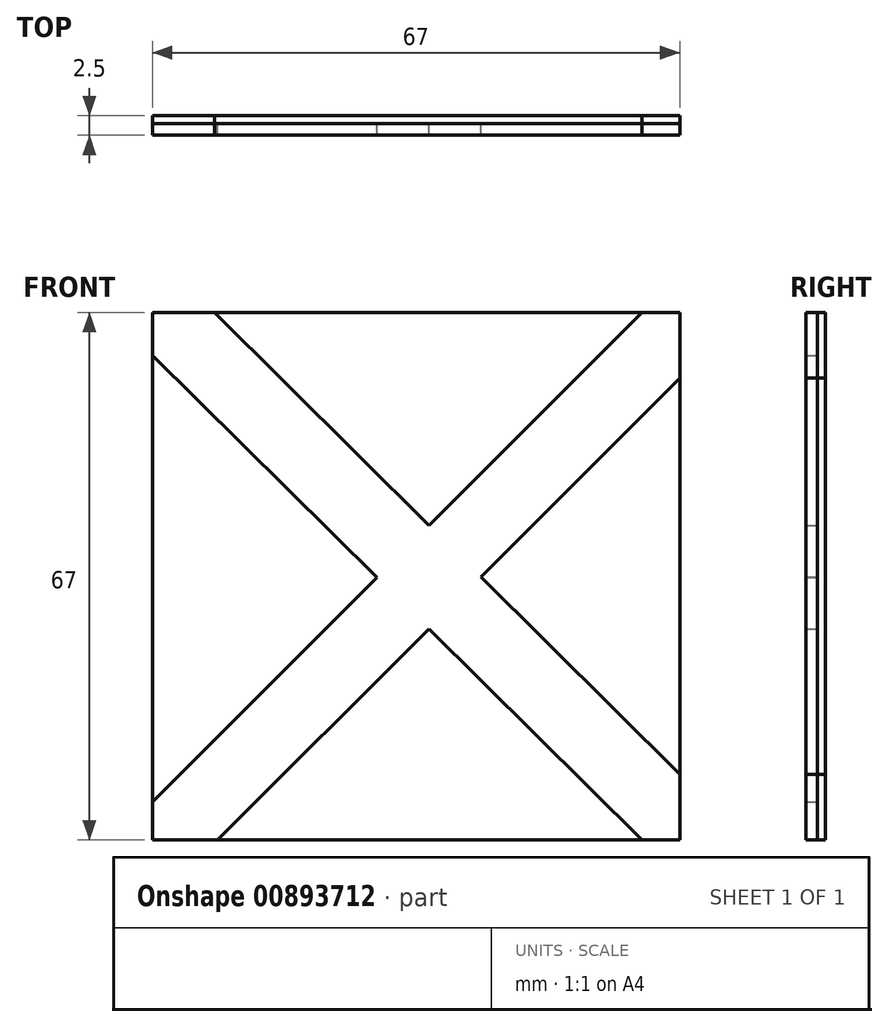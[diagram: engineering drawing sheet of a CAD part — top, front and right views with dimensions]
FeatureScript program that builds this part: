
annotation { "Feature Type Name" : "Feature", "Feature Type Description" : "" }
export const myFeature = defineFeature(function(context is Context, id is Id, definition is map)
    precondition{}
    {
        {
            var Q0;
            Q0=qCreatedBy(makeId("Front.planeOp"),FACE);
            var sketch = newSketch(context, id + "F0", { "sketchPlane" : qUnion([Q0])});
            skLineSegment(sketch, "E0.bottom", {"start": v(33.5, -33.5) * mm, "end": v(-33.5, -33.5) * mm});
            skLineSegment(sketch, "E0.top", {"start": v(33.5, 33.5) * mm, "end": v(-33.5, 33.5) * mm});
            skLineSegment(sketch, "E0.left", {"start": v(33.5, -33.5) * mm, "end": v(33.5, 33.5) * mm});
            skLineSegment(sketch, "E0.right", {"start": v(-33.5, -33.5) * mm, "end": v(-33.5, 33.5) * mm});
            skPoint(sketch, "E0.middle", {"position": v(0, 0) * mm});
            skLineSegment(sketch, "E1", {"start": v(-33.5, -28.7) * mm, "end": v(-4.98, -0.18) * mm});
            skLineSegment(sketch, "E2", {"start": v(-25.19, -33.5) * mm, "end": v(1.61, -6.7) * mm});
            skLineSegment(sketch, "E3", {"start": v(-33.5, 28.03) * mm, "end": v(-4.98, -0.18) * mm});
            skLineSegment(sketch, "E4", {"start": v(-25.6, 33.5) * mm, "end": v(1.64, 6.44) * mm});
            skLineSegment(sketch, "E5.trimOffspring", {"start": v(1.64, 6.44) * mm, "end": v(28.7, 33.5) * mm});
            skLineSegment(sketch, "E6.trimOffspring", {"start": v(1.61, -6.7) * mm, "end": v(28.7, -33.5) * mm});
            skLineSegment(sketch, "E7.trimOffspring", {"start": v(8.22, -0.1) * mm, "end": v(33.5, 25.19) * mm});
            skLineSegment(sketch, "E8.trimOffspring", {"start": v(8.22, -0.1) * mm, "end": v(33.5, -25.19) * mm});
            skSolve(sketch);
        }
        {
            var Q0;
            {var subQ0=sQuery(id+"F0.wireOp",EDGE,"E1");Q0=makeQuery(id+"F0.imprint","IMPRINT",FACE,{"disambiguationData":[TD([[makeQuery(id+"F0.imprint","IMPRINT",EDGE,{"derivedFrom":subQ0}),1.0]])]});}
            var Q1;
            {var subQ0=sQuery(id+"F0.wireOp",EDGE,"E4");Q1=makeQuery(id+"F0.imprint","IMPRINT",FACE,{"disambiguationData":[TD([[makeQuery(id+"F0.imprint","IMPRINT",EDGE,{"derivedFrom":subQ0}),1.0]])]});}
            var Q2;
            {var subQ0=sQuery(id+"F0.wireOp",EDGE,"E7.trimOffspring");Q2=makeQuery(id+"F0.imprint","IMPRINT",FACE,{"disambiguationData":[TD([[makeQuery(id+"F0.imprint","IMPRINT",EDGE,{"derivedFrom":subQ0}),-1.0]])]});}
            var Q3;
            {var subQ0=sQuery(id+"F0.wireOp",EDGE,"E2");Q3=makeQuery(id+"F0.imprint","IMPRINT",FACE,{"disambiguationData":[TD([[makeQuery(id+"F0.imprint","IMPRINT",EDGE,{"derivedFrom":subQ0}),-1.0]])]});}
            extrude(context, id + "F1", {"entities" : qUnion([Q0, Q1, Q2, Q3]), "depth" : 2.5 * mm, "offsetDistance" : 25.4 * mm});
        }
        {
            var Q0;
            Q0 = qSketchRegion(id + "F0", true);
            extrude(context, id + "F2", {"entities" : qUnion([Q0]), "depth" : 1 * mm, "offsetDistance" : 25.4 * mm});
        }
    });
